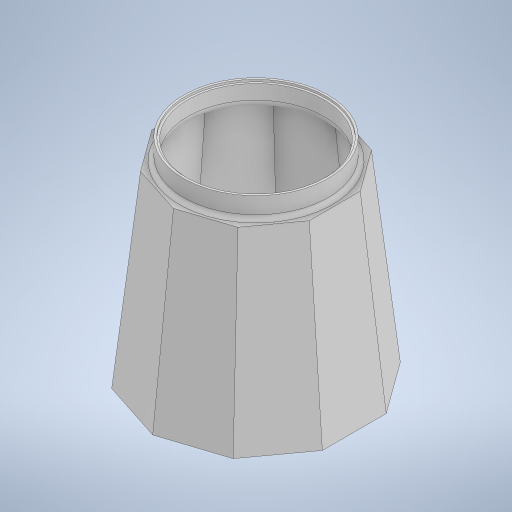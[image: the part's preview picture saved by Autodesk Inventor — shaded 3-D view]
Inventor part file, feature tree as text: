
AUTODESK INVENTOR PART (.ipt)
format: ipt  version: 2024 (Build 280153000, 153)  size: 347,648 bytes
history: native  units: mm
features: sketch x4, extrude x2, plane x1, loft x1, fillet x1, shell x1
ambient origin geometry x8: Origin, YZ Plane, XZ Plane, XY Plane, X Axis, Y Axis, Z Axis, Center Point
bodies: Solid1 (feature_tree)
feature tree (10):
  sketch  "Sketch3"  dims[d1=100.0mm d2=29.389263mm]
  plane  "Work Plane1"
  loft  "Loft1"
  extrude  "Extrusion1"  Depth=80.0mm
  fillet  "Fillet1"  Radius=23.525145mm
  shell  "Shell1"  Thickness=0.0mm
  extrude  "Extrusion2"  Depth=70.0mm
  sketch  "Sketch4"  dims[d3=90.0mm d4=80.0mm d5=23.525145mm d6=0.0mm d7=90.0deg]
  sketch  "Sketch6"  dims[d8=0.0mm d9=90.0deg d10=70.0mm]
  sketch  "Sketch7"  dims[d11=10.0mm d12=0.0mm d13=2.0mm d14=2.0mm d15=68.0mm d16=1.0mm d17=0.0mm]
